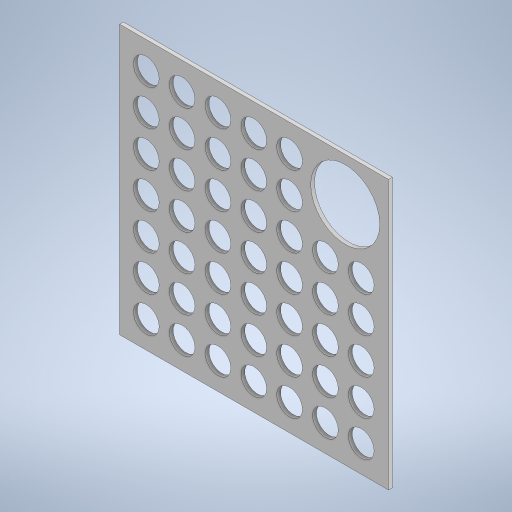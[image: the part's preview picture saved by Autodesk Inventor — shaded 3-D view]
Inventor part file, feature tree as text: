
AUTODESK INVENTOR PART (.ipt)
format: ipt  version: 2023 (Build 270158000, 158)  size: 360,448 bytes
history: native  units: mm
features: extrude x4, sketch x4, pattern_linear x2
ambient origin geometry x8: Origin, YZ Plane, XZ Plane, XY Plane, X Axis, Y Axis, Z Axis, Center Point
bodies: Solid1 (feature_tree)
feature tree (10):
  extrude  "Extrusion1"  Depth=214.0mm
  extrude  "Extrusion2"  Depth=3.0mm
  pattern_linear  "Rectangular Pattern1"  Count1=20  [1 undecoded]
  extrude  "Extrusion3"  Depth=28.5mm
  pattern_linear  "Rectangular Pattern2"  Spacing1=3.0mm  [1 undecoded]
  extrude  "Extrusion4"  Depth=3.0mm
  sketch  "Sketch1"  dims[d0=214.0mm d1=214.0mm]
  sketch  "Sketch2"  dims[d2=3.0mm d3=0.0mm d4=200.0mm d5=200.0mm]
  sketch  "Sketch3"  dims[d6=28.5mm d7=28.5mm]
  sketch  "Sketch4"  dims[d8=20.5mm d9=3.0mm d10=0.0mm d11=70.0mm d13=28.5mm d14=50.0mm d16=28.5mm d17=28.5mm d18=20.5mm d19=3.0mm d20=0.0mm d21=50.0mm d23=28.5mm d24=20.0mm d26=28.5mm d27=200.0mm d28=200.0mm d29=55.0mm d30=55.0mm d31=3.0mm d32=0.0mm]
note: 2 required parameter values undecoded (feature->parameter linkage not recoverable at this tier; creation-order binding heuristic only, values carry confidence <= 0.55)
